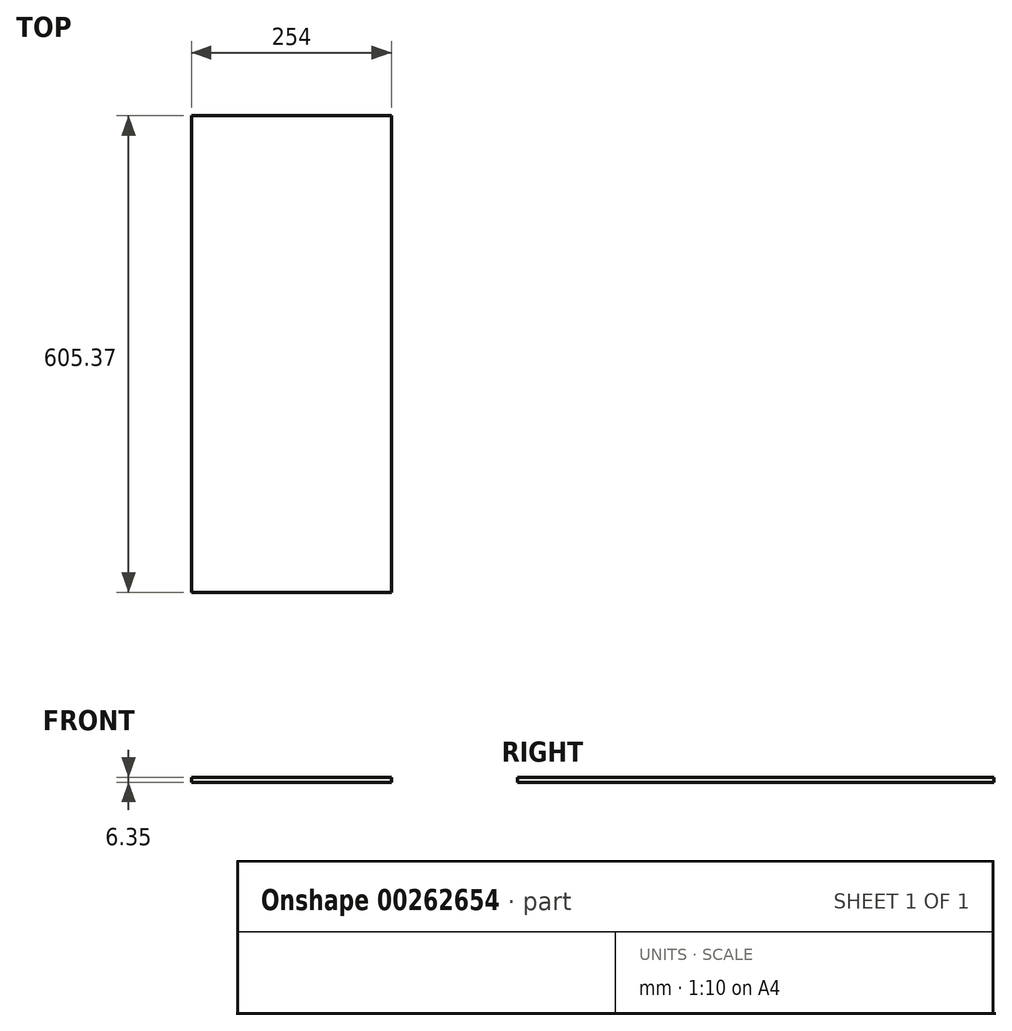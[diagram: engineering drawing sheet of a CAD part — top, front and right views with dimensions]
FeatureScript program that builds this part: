
annotation { "Feature Type Name" : "Feature", "Feature Type Description" : "" }
export const myFeature = defineFeature(function(context is Context, id is Id, definition is map)
    precondition{}
    {
        {
            var Q0;
            Q0=qCreatedBy(makeId("Top.planeOp"),FACE);
            var sketch = newSketch(context, id + "F0", { "sketchPlane" : qUnion([Q0])});
            skLineSegment(sketch, "E0.bottom", {"start": v(0, 0) * mm, "end": v(254, 0) * mm});
            skLineSegment(sketch, "E0.top", {"start": v(0, 605.37) * mm, "end": v(254, 605.37) * mm});
            skLineSegment(sketch, "E0.left", {"start": v(0, 0) * mm, "end": v(0, 605.37) * mm});
            skLineSegment(sketch, "E0.right", {"start": v(254, 0) * mm, "end": v(254, 605.37) * mm});
            skSolve(sketch);
        }
        {
            var Q0;
            Q0=makeQuery(id+"F0.imprint","IMPRINT",FACE,{"disambiguationData":[TD([[makeQuery(id+"F0.imprint","IMPRINT",EDGE,{"derivedFrom":sQuery(id+"F0.wireOp",EDGE,"E0.bottom")}),1.0]])]});
            extrude(context, id + "F1", {"entities" : qUnion([Q0]), "depth" : 6.35 * mm});
        }
    });
